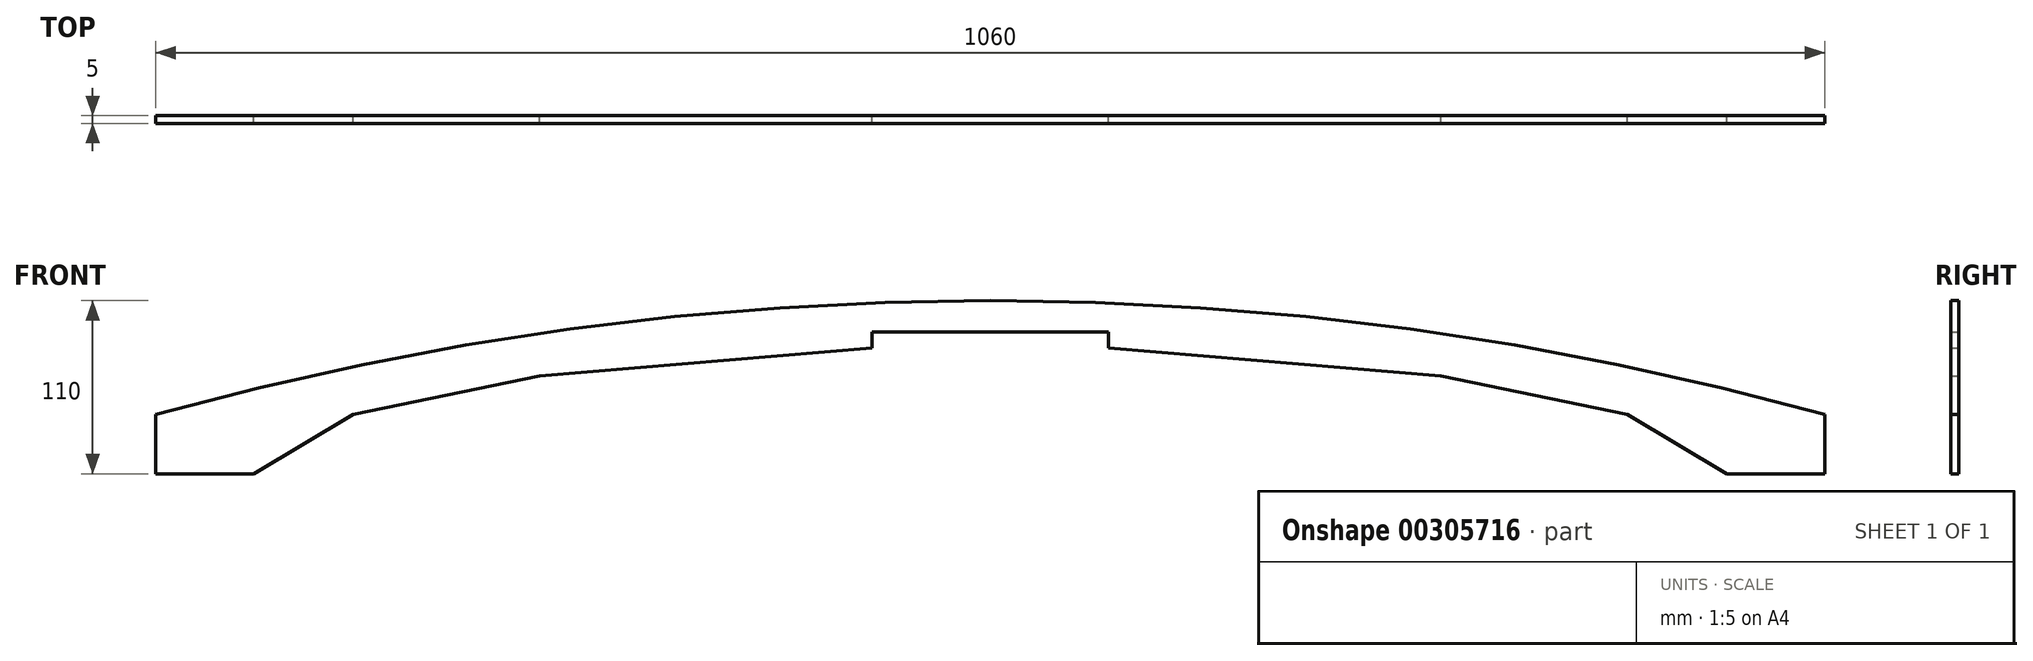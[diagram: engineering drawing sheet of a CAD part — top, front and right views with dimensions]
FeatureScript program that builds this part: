
annotation { "Feature Type Name" : "Feature", "Feature Type Description" : "" }
export const myFeature = defineFeature(function(context is Context, id is Id, definition is map)
    precondition{}
    {
        {
            var Q0;
            Q0=qCreatedBy(makeId("Front.planeOp"),FACE);
            var sketch = newSketch(context, id + "F0", { "sketchPlane" : qUnion([Q0])});
            skArc(sketch, "E0", {"start": v(650, 0) * mm, "mid": v(329.62, 82.3) * mm, "end": v(0, 110) * mm, "construction": true});
            skLineSegment(sketch, "E1", {"start": v(-650, 0) * mm, "end": v(-530, 0) * mm, "construction": true});
            skLineSegment(sketch, "E2", {"start": v(0, 0) * mm, "end": v(0, 90) * mm});
            skPoint(sketch, "E3.orphan", {"position": v(0, 0) * mm});
            skLineSegment(sketch, "E4", {"start": v(-75, 90) * mm, "end": v(0, 90) * mm});
            skLineSegment(sketch, "E5", {"start": v(-75, 90) * mm, "end": v(-75, 80) * mm});
            skLineSegment(sketch, "E6", {"start": v(75, 90) * mm, "end": v(75, 80) * mm, "construction": true});
            skLineSegment(sketch, "E7", {"start": v(-75, 80) * mm, "end": v(-286.14, 62.3) * mm});
            skLineSegment(sketch, "E8", {"start": v(-530, 37.57) * mm, "end": v(-530, 0) * mm});
            skArc(sketch, "E9", {"start": v(-530, 37.57) * mm, "mid": v(-590.3, 19.74) * mm, "end": v(-650, 0) * mm, "construction": true});
            skLineSegment(sketch, "E10", {"start": v(-530, 0) * mm, "end": v(-467.83, 0) * mm});
            skArc(sketch, "E11", {"start": v(0, 110) * mm, "mid": v(-267.46, 91.8) * mm, "end": v(-530, 37.57) * mm});
            skLineSegment(sketch, "E12", {"start": v(0, 0) * mm, "end": v(650, 0) * mm, "construction": true});
            skLineSegment(sketch, "E13", {"start": v(0, 90) * mm, "end": v(0, 110) * mm});
            skLineSegment(sketch, "E14", {"start": v(-467.83, 0) * mm, "end": v(0, 0) * mm, "construction": true});
            skLineSegment(sketch, "E15", {"start": v(-467.83, 0) * mm, "end": v(-404.67, 37.57) * mm});
            skLineSegment(sketch, "E16", {"start": v(-404.67, 37.57) * mm, "end": v(-286.14, 62.3) * mm});
            skLineSegment(sketch, "E17", {"start": v(0, 90) * mm, "end": v(75, 90) * mm, "construction": true});
            skSolve(sketch);
        }
        {
            var Q0;
            Q0=makeQuery(id+"F0.imprint","IMPRINT",FACE,{"disambiguationData":[TD([[makeQuery(id+"F0.imprint","IMPRINT",EDGE,{"derivedFrom":sQuery(id+"F0.wireOp",EDGE,"E4")}),1.0]])]});
            extrude(context, id + "F1", {"entities" : qUnion([Q0]), "endBound" : BoundingType.SYMMETRIC, "depth" : 5 * mm});
        }
        {
            var Q0;
            Q0=makeQuery(id+"F1.opExtrude","SWEPT_BODY",BODY,{"disambiguationData":[OSD([sQuery(id+"F0.wireOp",EDGE,"E4"),sQuery(id+"F0.wireOp",EDGE,"E5"),sQuery(id+"F0.wireOp",EDGE,"E7"),sQuery(id+"F0.wireOp",EDGE,"E8"),sQuery(id+"F0.wireOp",EDGE,"E10"),sQuery(id+"F0.wireOp",EDGE,"E11"),sQuery(id+"F0.wireOp",EDGE,"E13"),sQuery(id+"F0.wireOp",EDGE,"E15"),sQuery(id+"F0.wireOp",EDGE,"E16")])]});
            var Q1;
            Q1=qCreatedBy(makeId("Right.planeOp"),FACE);
            mirror(context, id + "F2", {"operationType" : NewBodyOperationType.ADD, "entities" : qUnion([Q0]), "mirrorPlane" : qUnion([Q1])});
        }
    });
